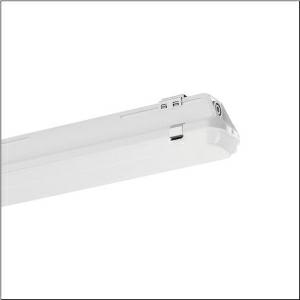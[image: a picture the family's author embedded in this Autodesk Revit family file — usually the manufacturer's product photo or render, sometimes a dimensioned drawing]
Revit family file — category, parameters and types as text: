
# Revit family: monsun_r__12_51fp107p460h_794b
name_source: partatom
category: Lighting Fixtures
units: mm (PartAtom-declared; Revit-internal decimal feet)

## family parameters
Cut with Voids When Loaded = No
Host = Face
Light Source = No
Part Type = Normal
Room Calculation Point = No
Round Connector Dimension = Use Diameter
Shared = No

## types (1)
- Monsun® 12 (1 x LED, 5800 lm, 32.5 W, 4000K)
    Apparent Load = 33 VA
    CIE Flux Codes = 47 77 93 94 100
    Color Rendering = 80
    Color Temperature = 4000K
    Default Elevation = 1800 mm
    Description = Monsun® 12, damp-proof luminaire, chain hanger, primary optical cover: enclosure, of PMMA, light emission: direct distribution, primary light characteristic: symmetric, installation type: suspended mounting, surface-mounted, horizontal mounting, vertical mounting, LED rated luminous flux: 5.800 lm, light colour: 840, colour temperature: 4000K, control gear: ECG, with terminal, 3-pole, max. 2.5mm², mains connection: 220..240V, AC, 50/60Hz, rated input power: 33W, luminaire housing, of glass-fibre reinforced polyester, uncoated, bright grey, length: 1.590 mm, width: 90 mm, height: 88mm, clip for enclosure, of stainless steel (V2A), ceiling mounting element, of stainless steel (V2A), chain hanger, of stainless steel (V2A), protection rating (complete): IP66, insulation class (complete): insulation class I (protective earthing), certification: CE, ENEC, VDE, protection symbol: D, impact resistance: IK04, permissible ambient temperature for indoor applications: -35..+40°C, standard: EN 50419, EN 60598-2-1, no direct snow, no direct sun, no direct rain, for indoor or canopied outdoor use, corresponds to IFS (International Featured Standards) requirements for safety and quality in the food industry, for animal farming (ammonia tested): for use in cowhouse, pig house, horse-stables... (not for use in poultry stables), AT max for animal farming = 40°C, packaging unit: 1 piece
    Height = 89 mm
    Lamp = 1 x LED
    Lamp Light Flux = 5800 lm
    Lamp Power = 32.5 W
    Lamp count = 1
    Length = 1590 mm
    Luminous efficacy = 178 lm/W
    Manufacturer = Siteco
    ModVariant = No
    Model = 51FP107P460H
    Mounting Place = Ceiling
    Mounting Type = Pendant
    Number of Poles = 1
    OnlyDefault = Yes
    Power Factor = 1
    Product Name = Monsun® 12
    Product group = damp-proof luminaire | ceiling pendant
    ProductGroupID = 908
    Protection Class = Protection class I
    Protection Degree = IP 66
    RLX_Detail_Level = 1
    RlxData = <blob elided: 88325 chars, md5=e32d377d>
    Socket = socket
    Standby Power = 0 W
    System Light Flux = 5800 lm
    System Power = 33 W
    Type Comments = Product without accessories
    Type Image = l_1004748.jpg
    URL = http://relux.com
    VarID = ---
    Voltage = 0 V
    Weight = 0.00 kg
    Width = 90 mm

## geometry (parser evidence)
native form markers: Blend x4, Sweep x12
no freeform markers — native parametric forms only
